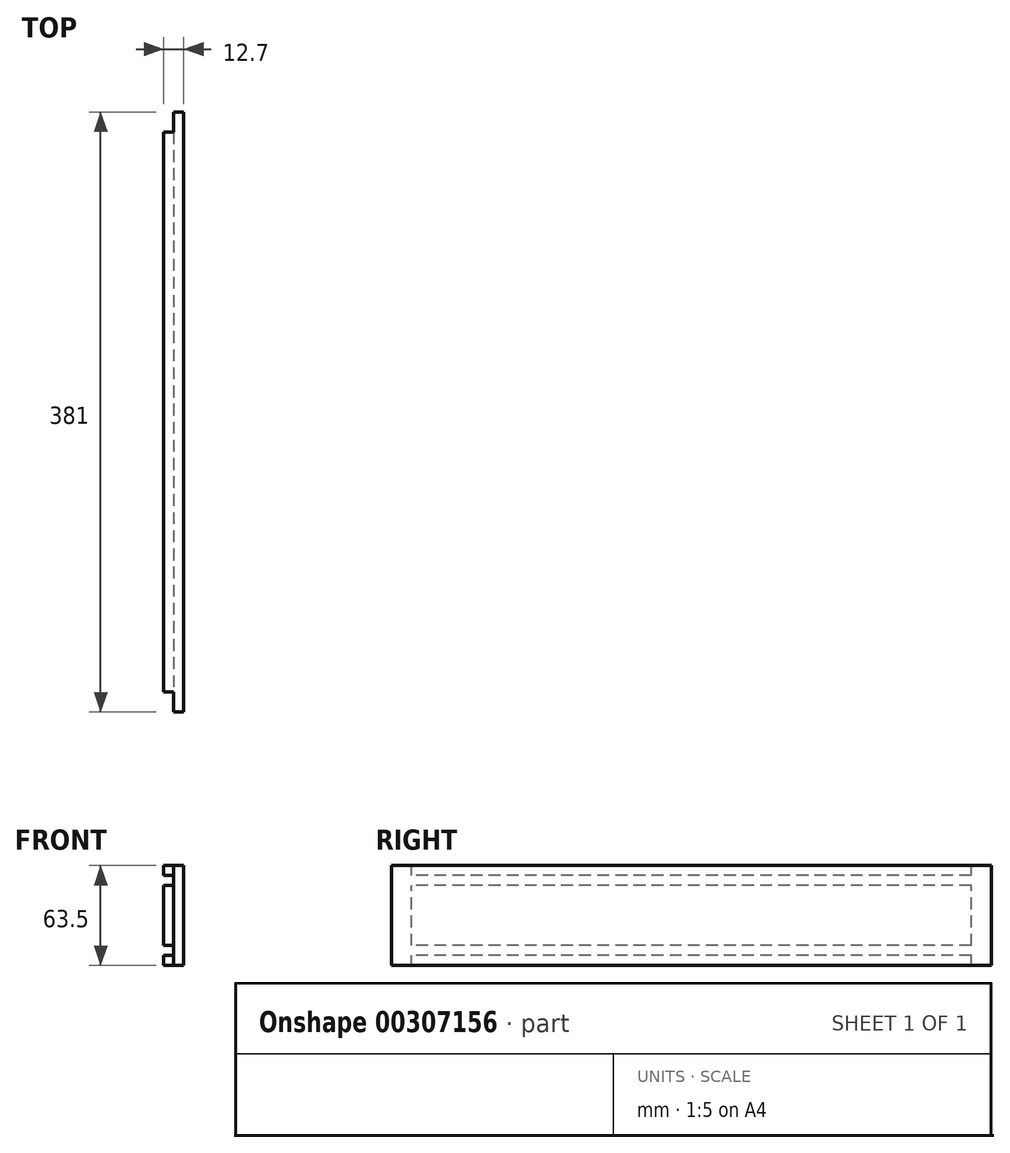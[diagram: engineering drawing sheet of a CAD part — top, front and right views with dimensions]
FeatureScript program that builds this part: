
annotation { "Feature Type Name" : "Feature", "Feature Type Description" : "" }
export const myFeature = defineFeature(function(context is Context, id is Id, definition is map)
    precondition{}
    {
        {
            var Q0;
            Q0=qCreatedBy(makeId("Right.planeOp"),FACE);
            var sketch = newSketch(context, id + "F0", { "sketchPlane" : qUnion([Q0])});
            skLineSegment(sketch, "E0.bottom", {"start": v(193.37, -31.75) * mm, "end": v(-187.63, -31.75) * mm});
            skLineSegment(sketch, "E0.top", {"start": v(193.37, 31.75) * mm, "end": v(-187.63, 31.75) * mm});
            skLineSegment(sketch, "E0.left", {"start": v(193.37, -31.75) * mm, "end": v(193.37, 31.75) * mm});
            skLineSegment(sketch, "E0.right", {"start": v(-187.63, -31.75) * mm, "end": v(-187.63, 31.75) * mm});
            skPoint(sketch, "E0.middle", {"position": v(2.87, 0) * mm});
            skSolve(sketch);
        }
        {
            var Q0;
            Q0=makeQuery(id+"F0.imprint","IMPRINT",FACE,{"disambiguationData":[TD([[makeQuery(id+"F0.imprint","IMPRINT",EDGE,{"derivedFrom":sQuery(id+"F0.wireOp",EDGE,"E0.bottom")}),-1.0]])]});
            extrude(context, id + "F1", {"entities" : qUnion([Q0]), "depth" : 12.7 * mm});
        }
        {
            var Q0;
            Q0=makeQuery(id+"F1.opExtrude","CAP_FACE",FACE,{"disambiguationData":[OSD([sQuery(id+"F0.wireOp",EDGE,"E0.bottom"),sQuery(id+"F0.wireOp",EDGE,"E0.top"),sQuery(id+"F0.wireOp",EDGE,"E0.left"),sQuery(id+"F0.wireOp",EDGE,"E0.right")])],"isStart":true});
            var sketch = newSketch(context, id + "F2", { "sketchPlane" : qUnion([Q0])});
            skLineSegment(sketch, "E1.bottom", {"start": v(-193.37, 25.4) * mm, "end": v(187.63, 25.4) * mm});
            skLineSegment(sketch, "E1.top", {"start": v(-193.37, 19.05) * mm, "end": v(187.63, 19.05) * mm});
            skLineSegment(sketch, "E1.left", {"start": v(-193.37, 25.4) * mm, "end": v(-193.37, 19.05) * mm});
            skLineSegment(sketch, "E1.right", {"start": v(187.63, 25.4) * mm, "end": v(187.63, 19.05) * mm});
            skLineSegment(sketch, "E2.bottom", {"start": v(-193.37, -19.05) * mm, "end": v(187.63, -19.05) * mm});
            skLineSegment(sketch, "E2.top", {"start": v(-193.37, -25.4) * mm, "end": v(187.63, -25.4) * mm});
            skLineSegment(sketch, "E2.left", {"start": v(-193.37, -19.05) * mm, "end": v(-193.37, -25.4) * mm});
            skLineSegment(sketch, "E2.right", {"start": v(187.63, -19.05) * mm, "end": v(187.63, -25.4) * mm});
            skSolve(sketch);
        }
        {
            var Q0;
            Q0=makeQuery(id+"F2.imprint","IMPRINT",FACE,{"disambiguationData":[TD([[makeQuery(id+"F2.imprint","IMPRINT",EDGE,{"derivedFrom":sQuery(id+"F2.wireOp",EDGE,"E1.bottom")}),-1.0]])]});
            var Q1;
            Q1=makeQuery(id+"F2.imprint","IMPRINT",FACE,{"disambiguationData":[TD([[makeQuery(id+"F2.imprint","IMPRINT",EDGE,{"derivedFrom":sQuery(id+"F2.wireOp",EDGE,"E2.bottom")}),-1.0]])]});
            extrude(context, id + "F3", {"entities" : qUnion([Q0, Q1]), "operationType" : NewBodyOperationType.REMOVE, "oppositeDirection" : true, "depth" : 6.35 * mm});
        }
        {
            var Q0;
            Q0=makeQuery(id+"F1.opExtrude","SWEPT_FACE",FACE,{"disambiguationData":[OSD([sQuery(id+"F0.wireOp",EDGE,"E0.top")])]});
            var sketch = newSketch(context, id + "F4", { "sketchPlane" : qUnion([Q0])});
            skLineSegment(sketch, "E3.bottom", {"start": v(6.35, -187.63) * mm, "end": v(0, -187.63) * mm});
            skLineSegment(sketch, "E3.top", {"start": v(6.35, -174.93) * mm, "end": v(0, -174.93) * mm});
            skLineSegment(sketch, "E3.left", {"start": v(6.35, -187.63) * mm, "end": v(6.35, -174.93) * mm});
            skLineSegment(sketch, "E3.right", {"start": v(0, -187.63) * mm, "end": v(0, -174.93) * mm});
            skLineSegment(sketch, "E4.bottom", {"start": v(6.35, 193.37) * mm, "end": v(0, 193.37) * mm});
            skLineSegment(sketch, "E4.top", {"start": v(6.35, 180.67) * mm, "end": v(0, 180.67) * mm});
            skLineSegment(sketch, "E4.left", {"start": v(6.35, 193.37) * mm, "end": v(6.35, 180.67) * mm});
            skLineSegment(sketch, "E4.right", {"start": v(0, 193.37) * mm, "end": v(0, 180.67) * mm});
            skSolve(sketch);
        }
        {
            var Q0;
            Q0=makeQuery(id+"F4.imprint","IMPRINT",FACE,{"disambiguationData":[TD([[makeQuery(id+"F4.imprint","IMPRINT",EDGE,{"derivedFrom":sQuery(id+"F4.wireOp",EDGE,"E4.bottom")}),1.0]])]});
            var Q1;
            Q1=makeQuery(id+"F4.imprint","IMPRINT",FACE,{"disambiguationData":[TD([[makeQuery(id+"F4.imprint","IMPRINT",EDGE,{"derivedFrom":sQuery(id+"F4.wireOp",EDGE,"E3.bottom")}),-1.0]])]});
            extrude(context, id + "F5", {"entities" : qUnion([Q0, Q1]), "operationType" : NewBodyOperationType.REMOVE, "endBound" : BoundingType.THROUGH_ALL, "oppositeDirection" : true, "depth" : 25.4 * mm});
        }
    });
